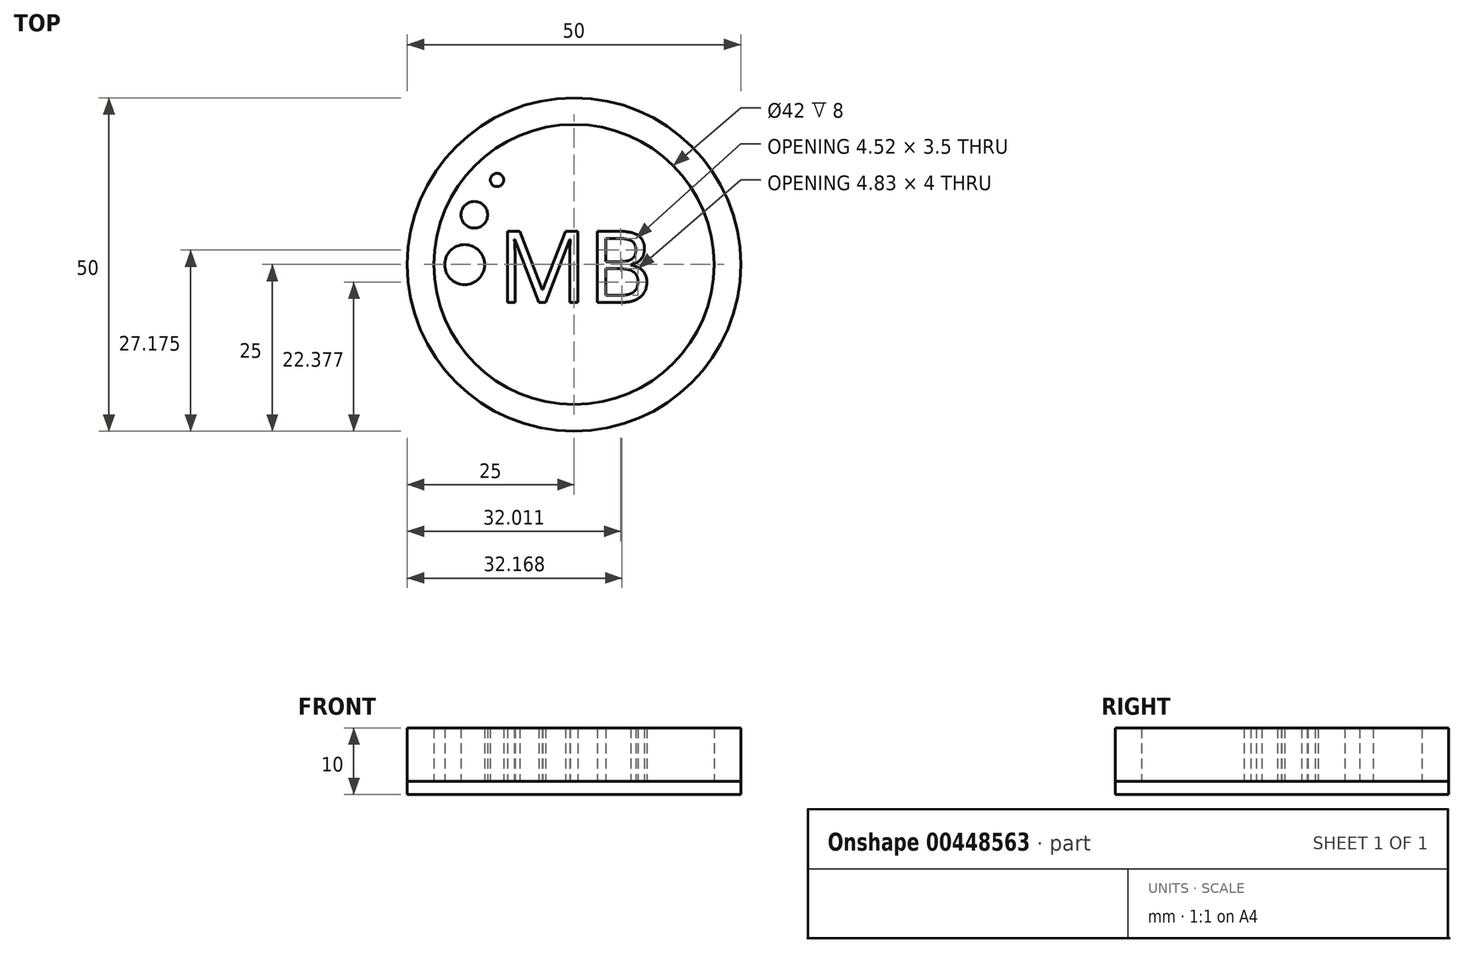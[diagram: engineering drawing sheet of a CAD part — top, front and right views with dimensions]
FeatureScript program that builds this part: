
annotation { "Feature Type Name" : "Feature", "Feature Type Description" : "" }
export const myFeature = defineFeature(function(context is Context, id is Id, definition is map)
    precondition{}
    {
        {
            var Q0;
            Q0=qCreatedBy(makeId("Top.planeOp"),FACE);
            var sketch = newSketch(context, id + "F0", { "sketchPlane" : qUnion([Q0])});
            skCircle(sketch, "E0", {"center": v(0, 0) * mm, "radius": 25 * mm});
            skCircle(sketch, "E1", {"center": v(0, 0) * mm, "radius": 21 * mm});
            skCircle(sketch, "E2", {"center": v(-11.55, 12.68) * mm, "radius": 1 * mm});
            skCircle(sketch, "E3", {"center": v(-14.95, 7.46) * mm, "radius": 2 * mm});
            skCircle(sketch, "E4", {"center": v(-16.4, -0.02) * mm, "radius": 3 * mm});
            skText(sketch, "E5", { "text": "MB", "fontName": "OpenSans-Regular.ttf"});
            const initialGuessF0  = {"E5": [-0.01146, -0.00568, 1, 0, 0.01077]};
            skSetInitialGuess(sketch, initialGuessF0);
            skSolve(sketch);
        }
        {
            var Q0;
            Q0 = qSketchRegion(id + "F0", true);
            var Q1;
            Q1=makeQuery(id+"F0.imprint","IMPRINT",FACE,{"disambiguationData":[TD([[makeQuery(id+"F0.imprint","IMPRINT",EDGE,{"derivedFrom":sQuery(id+"F0.wireOp",EDGE,"E5.sketch_text.stroke-18")}),-1.0]])]});
            var Q2;
            Q2=makeQuery(id+"F0.imprint","IMPRINT",FACE,{"disambiguationData":[TD([[makeQuery(id+"F0.imprint","IMPRINT",EDGE,{"derivedFrom":sQuery(id+"F0.wireOp",EDGE,"E5.sketch_text.stroke-0")}),-1.0]])]});
            var Q3;
            Q3=makeQuery(id+"F0.imprint","IMPRINT",FACE,{"disambiguationData":[TD([[makeQuery(id+"F0.imprint","IMPRINT",EDGE,{"derivedFrom":sQuery(id+"F0.wireOp",EDGE,"E3")}),1.0]])]});
            var Q4;
            Q4=makeQuery(id+"F0.imprint","IMPRINT",FACE,{"disambiguationData":[TD([[makeQuery(id+"F0.imprint","IMPRINT",EDGE,{"derivedFrom":sQuery(id+"F0.wireOp",EDGE,"E2")}),1.0]])]});
            var Q5;
            Q5=makeQuery(id+"F0.imprint","IMPRINT",FACE,{"disambiguationData":[TD([[makeQuery(id+"F0.imprint","IMPRINT",EDGE,{"derivedFrom":sQuery(id+"F0.wireOp",EDGE,"E4")}),1.0]])]});
            extrude(context, id + "F1", {"entities" : qUnion([Q0, Q1, Q2, Q3, Q4, Q5]), "depth" : 8 * mm});
        }
        {
            var Q0;
            Q0=qCreatedBy(makeId("Top.planeOp"),FACE);
            var sketch = newSketch(context, id + "F2", { "sketchPlane" : qUnion([Q0])});
            skCircle(sketch, "E6", {"center": v(0, 0) * mm, "radius": 25 * mm});
            skSolve(sketch);
        }
        {
            var Q0;
            Q0 = qSketchRegion(id + "F2", true);
            extrude(context, id + "F3", {"entities" : qUnion([Q0]), "oppositeDirection" : true, "depth" : 2 * mm});
        }
    });
